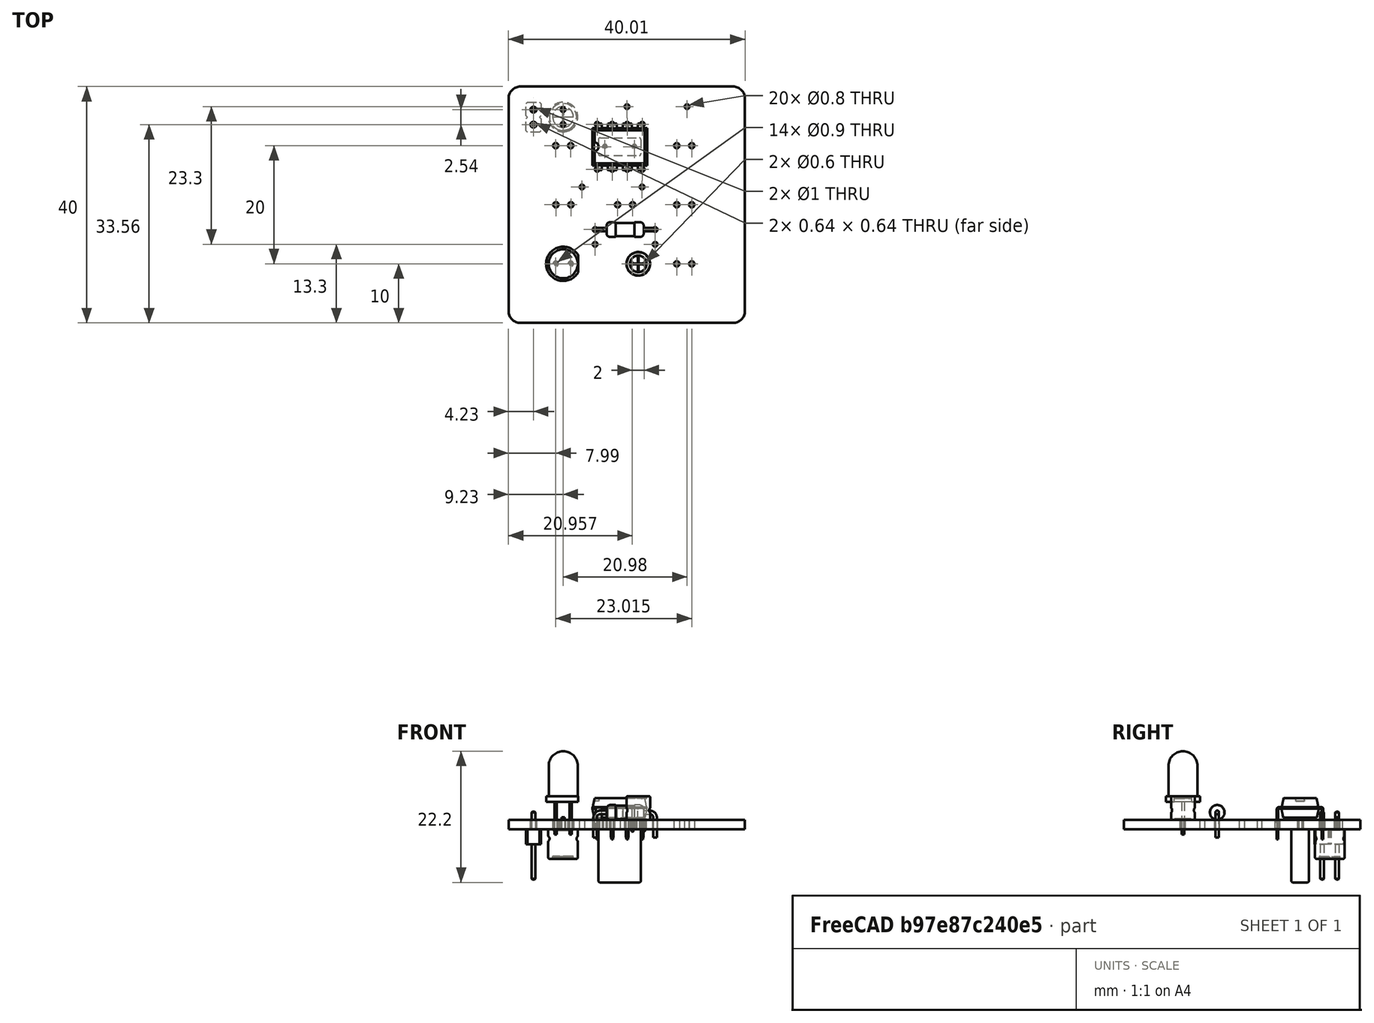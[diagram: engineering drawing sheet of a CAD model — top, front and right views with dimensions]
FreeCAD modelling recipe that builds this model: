
FCSTD DOCUMENT  (FreeCAD 0.19R24291 (Git))
Label: PCB-De-Elec-THT
License: All rights reserved
LicenseURL: http://en.wikipedia.org/wiki/All_rights_reserved
objects: Part::Feature×13, App::Link×9, App::Part×5, PartDesign::CoordinateSystem×1, Sketcher::SketchObject×1
note: 15 computed .brp shape members not serialized (recipe doc carries the construction recipe); baked Part::Feature solids carry a one-line shape summary decoded from their .brp

FEATURE [PartDesign::CoordinateSystem] Local_CS_6ee0
  AttacherType = Attacher::AttachEngine3D
FEATURE [Part::Feature] Pcb_6ee0
  shape: bbox 40 x 40 x 1.6 mm, 48 faces (baked)
FEATURE [Sketcher::SketchObject] PCB_Sketch_6ee0
  FullyConstrained = false
  sketch-geometry (8):
    g0: LineSegment StartX=120.175 StartY=-108 StartZ=0 EndX=120.175 EndY=-72 EndZ=0
    g1: LineSegment StartX=122.175 StartY=-70 StartZ=0 EndX=158.175 EndY=-70 EndZ=0
    g2: LineSegment StartX=160.175 StartY=-72 StartZ=0 EndX=160.175 EndY=-108 EndZ=0
    g3: LineSegment StartX=158.175 StartY=-110 StartZ=0 EndX=122.175 EndY=-110 EndZ=0
    g4: ArcOfCircle CenterX=158.175 CenterY=-108 CenterZ=0 NormalX=0 NormalY=0 NormalZ=1 AngleXU=0 Radius=2 StartAngle=4.71239 EndAngle=6.28319
    g5: ArcOfCircle CenterX=122.175 CenterY=-108 CenterZ=0 NormalX=0 NormalY=0 NormalZ=1 AngleXU=0 Radius=2 StartAngle=3.14159 EndAngle=4.71239
    g6: ArcOfCircle CenterX=122.175 CenterY=-72 CenterZ=0 NormalX=0 NormalY=0 NormalZ=1 AngleXU=0 Radius=2 StartAngle=1.5708 EndAngle=3.14159
    g7: ArcOfCircle CenterX=158.175 CenterY=-72 CenterZ=0 NormalX=0 NormalY=0 NormalZ=1 AngleXU=0 Radius=2 StartAngle=0 EndAngle=1.5708
  constraints (8):
    c: Coincident(g0,g5)
    c: Coincident(g0,g6)
    c: Coincident(g3,g5)
    c: Coincident(g1,g6)
    c: Coincident(g3,g4)
    c: Coincident(g1,g7)
    c: Coincident(g2,g4)
    c: Coincident(g2,g7)
FEATURE [Part::Feature] Shape  label="D3_LED_D5.0mm_Clear_c8d51a1c0c0e"
  Placement = pos=(130.7,-100,0) rot=(0,0,1;3.14159rad)
  shape: bbox 5.4 x 5.8 x 14.1 mm, 16 faces (baked)
FEATURE [Part::Feature] Shape001  label="U1_DIP-8_W7.62mm_69495754b2d9"
  Placement = pos=(135.175,-84,0) rot=(0,0,1;1.5708rad)
  shape: bbox 9.27 x 7.874 x 6.98 mm, 148 faces (baked)
FEATURE [Part::Feature] Shape002  label="R3_R_Axial_DIN0207_L63mm_D25mm_P1016mm_Horizontal_48222e3e548a"
  Placement = pos=(134.82,-94.2,0) rot=(0,0,1;0rad)
  shape: bbox 10.96 x 2.706 x 5.603 mm, 17 faces (baked)
FEATURE [App::Link] D3_LED_D5_0mm_Clear_c8d51a1c0c0e_ln_  label="D7_LED_D5.0mm_Clear_4a90934450c0"
  LinkPlacement = pos=(151.175,-100,0) rot=(0,0,1;3.14159rad)
  LinkedObject = -> Shape
  Placement = pos=(151.175,-100,0) rot=(0,0,1;3.14159rad)
FEATURE [App::Link] D3_LED_D5_0mm_Clear_c8d51a1c0c0e_ln_001  label="D5_LED_D5.0mm_Clear_5ddd5152daf8"
  LinkPlacement = pos=(151.175,-80,0) rot=(0,0,1;3.14159rad)
  LinkedObject = -> Shape
  Placement = pos=(151.175,-80,0) rot=(0,0,1;3.14159rad)
FEATURE [App::Link] D3_LED_D5_0mm_Clear_c8d51a1c0c0e_ln_002  label="D2_LED_D5.0mm_Clear_5184b244e816"
  LinkPlacement = pos=(130.725,-90,0) rot=(0,0,1;3.14159rad)
  LinkedObject = -> Shape
  Placement = pos=(130.725,-90,0) rot=(0,0,1;3.14159rad)
FEATURE [App::Link] D3_LED_D5_0mm_Clear_c8d51a1c0c0e_ln_003  label="D1_LED_D5.0mm_Clear_e87da6dd50d9"
  LinkPlacement = pos=(130.7,-80,0) rot=(0,0,1;3.14159rad)
  LinkedObject = -> Shape
  Placement = pos=(130.7,-80,0) rot=(0,0,1;3.14159rad)
FEATURE [App::Link] D3_LED_D5_0mm_Clear_c8d51a1c0c0e_ln_004  label="D6_LED_D5.0mm_Clear_5b6fce8f8c4e"
  LinkPlacement = pos=(151.175,-90,0) rot=(0,0,1;3.14159rad)
  LinkedObject = -> Shape
  Placement = pos=(151.175,-90,0) rot=(0,0,1;3.14159rad)
FEATURE [App::Link] R3_R_Axial_DIN0207_L63mm_D25mm_P1016mm_Horizontal_48222e3e548a_ln_  label="R2_R_Axial_DIN0207_L63mm_D25mm_P1016mm_Horizontal_e7e1008d464a"
  LinkPlacement = pos=(140.22,-73.4,0) rot=(0,0,1;0rad)
  LinkedObject = -> Shape002
  Placement = pos=(140.22,-73.4,0) rot=(0,0,1;0rad)
FEATURE [App::Link] R3_R_Axial_DIN0207_L63mm_D25mm_P1016mm_Horizontal_48222e3e548a_ln_001  label="R4_R_Axial_DIN0207_L63mm_D25mm_P1016mm_Horizontal_71a87f45e4ca"
  LinkPlacement = pos=(134.82,-96.7,0) rot=(0,0,1;0rad)
  LinkedObject = -> Shape002
  Placement = pos=(134.82,-96.7,0) rot=(0,0,1;0rad)
FEATURE [Part::Feature] Shape003  label="SW1_CP_Radial_D40mm_P200mm_0d74ae5376be"
  Placement = pos=(141.127,-100,0) rot=(0,0,1;0rad)
  shape: bbox 4.924 x 5.212 x 6 mm, 54 faces (baked)
FEATURE [App::Link] D3_LED_D5_0mm_Clear_c8d51a1c0c0e_ln_005  label="D4_LED_D5.0mm_Clear_6e587904ef55"
  LinkPlacement = pos=(141.175,-90,0) rot=(0,0,1;3.14159rad)
  LinkedObject = -> Shape
  Placement = pos=(141.175,-90,0) rot=(0,0,1;3.14159rad)
FEATURE [App::Link] R3_R_Axial_DIN0207_L63mm_D25mm_P1016mm_Horizontal_48222e3e548a_ln_002  label="R1_R_Axial_DIN0207_L63mm_D25mm_P1016mm_Horizontal_78fa2784fb1b"
  LinkPlacement = pos=(142.78,-87,0) rot=(0,0,1;3.14159rad)
  LinkedObject = -> Shape002
  Placement = pos=(142.78,-87,0) rot=(0,0,1;3.14159rad)
FEATURE [App::Part] Top_6ee0
  Group = -> [Shape,Shape001,Shape002,D3_LED_D5_0mm_Clear_c8d51a1c0c0e_ln_,D3_LED_D5_0mm_Clear_c8d51a1c0c0e_ln_001,D3_LED_D5_0mm_Clear_c8d51a1c0c0e_ln_002,D3_LED_D5_0mm_Clear_c8d51a1c0c0e_ln_003,D3_LED_D5_0mm_Clear_c8d51a1c0c0e_ln_004,R3_R_Axial_DIN0207_L63mm_D25mm_P1016mm_Horizontal_48222e3e548a_ln_,R3_R_Axial_DIN0207_L63mm_D25mm_P1016mm_Horizontal_48222e3e548a_ln_001,Shape003,+2 more]
  Origin = -> Origin003
FEATURE [Part::Feature] Shape004  label="C2_C_Rect_L72mm_W30mm_P500mm_FKS2_FKP2_MKS2_MKP2_9a8d65592bbd"
  Placement = pos=(136.475,-80.175,-1.6) rot=(1,0,0;3.14159rad)
  shape: bbox 7.2 x 3 x 10.9 mm, 22 faces (baked)
FEATURE [Part::Feature] Shape005  label="J1_PinHeader_1x02_P254mm_Vertical_77a5e3965d3b"
  Placement = pos=(124.4,-73.9,-1.6) rot=(0,1,0;3.14159rad)
  shape: bbox 2.54 x 5.08 x 11.54 mm, 52 faces (baked)
FEATURE [Part::Feature] Shape007  label="C1_CP_Radial_D50mm_P250mm_6f870ca8c2a1"
  Placement = pos=(129.4,-73.8949,-1.6) rot=(0.707107,-0.707107,0;3.14159rad)
  shape: bbox 6.515 x 6.128 x 7 mm, 49 faces (baked)
FEATURE [App::Part] Bot_6ee0
  Group = -> [Shape004,Shape005,Shape007]
  Origin = -> Origin004
FEATURE [App::Part] Step_Models_6ee0
  Group = -> [Top_6ee0,Bot_6ee0]
  Origin = -> Origin002
FEATURE [Part::Feature] tracks_area001  label="topTracks_6ee0"
  Placement = pos=(0,0,0.01) rot=(0,0,1;0rad)
  shape: bbox 6.3 x 2.9 x 2e-07 mm, 23 faces, 0 solids (baked)
FEATURE [Part::Feature] topPads_6ee0_  label="topPads_6ee0"
  Placement = pos=(0,0,0.02) rot=(0,0,1;0rad)
  shape: bbox 28.53 x 34.9 x 2e-07 mm, 42 faces, 0 solids (baked)
FEATURE [Part::Feature] tracks_area002  label="botTracks_6ee0"
  Placement = pos=(0,0,-1.61) rot=(0,0,1;0rad)
  shape: bbox 34.2 x 37.3 x 2e-07 mm, 140 faces, 0 solids (baked)
FEATURE [Part::Feature] zones_area001  label="botZones_6ee0"
  Placement = pos=(0,0,-1.61) rot=(0,0,1;0rad)
  shape: bbox 35.57 x 39.05 x 2e-07 mm, 3 faces, 0 solids (baked)
FEATURE [Part::Feature] botPads_6ee0_  label="botPads_6ee0"
  Placement = pos=(0,0,-1.62) rot=(0,0,1;0rad)
  shape: bbox 28.53 x 34.9 x 2e-07 mm, 42 faces, 0 solids (baked)
FEATURE [App::Part] Board_Geoms_6ee0
  Group = -> [Local_CS_6ee0,Pcb_6ee0,PCB_Sketch_6ee0,topPads_6ee0_,tracks_area001,botPads_6ee0_,tracks_area002,zones_area001]
  Origin = -> Origin
FEATURE [App::Part] Board_6ee0  label="CAO-Kicad"
  Group = -> [Board_Geoms_6ee0,Step_Models_6ee0]
  Origin = -> Origin001
